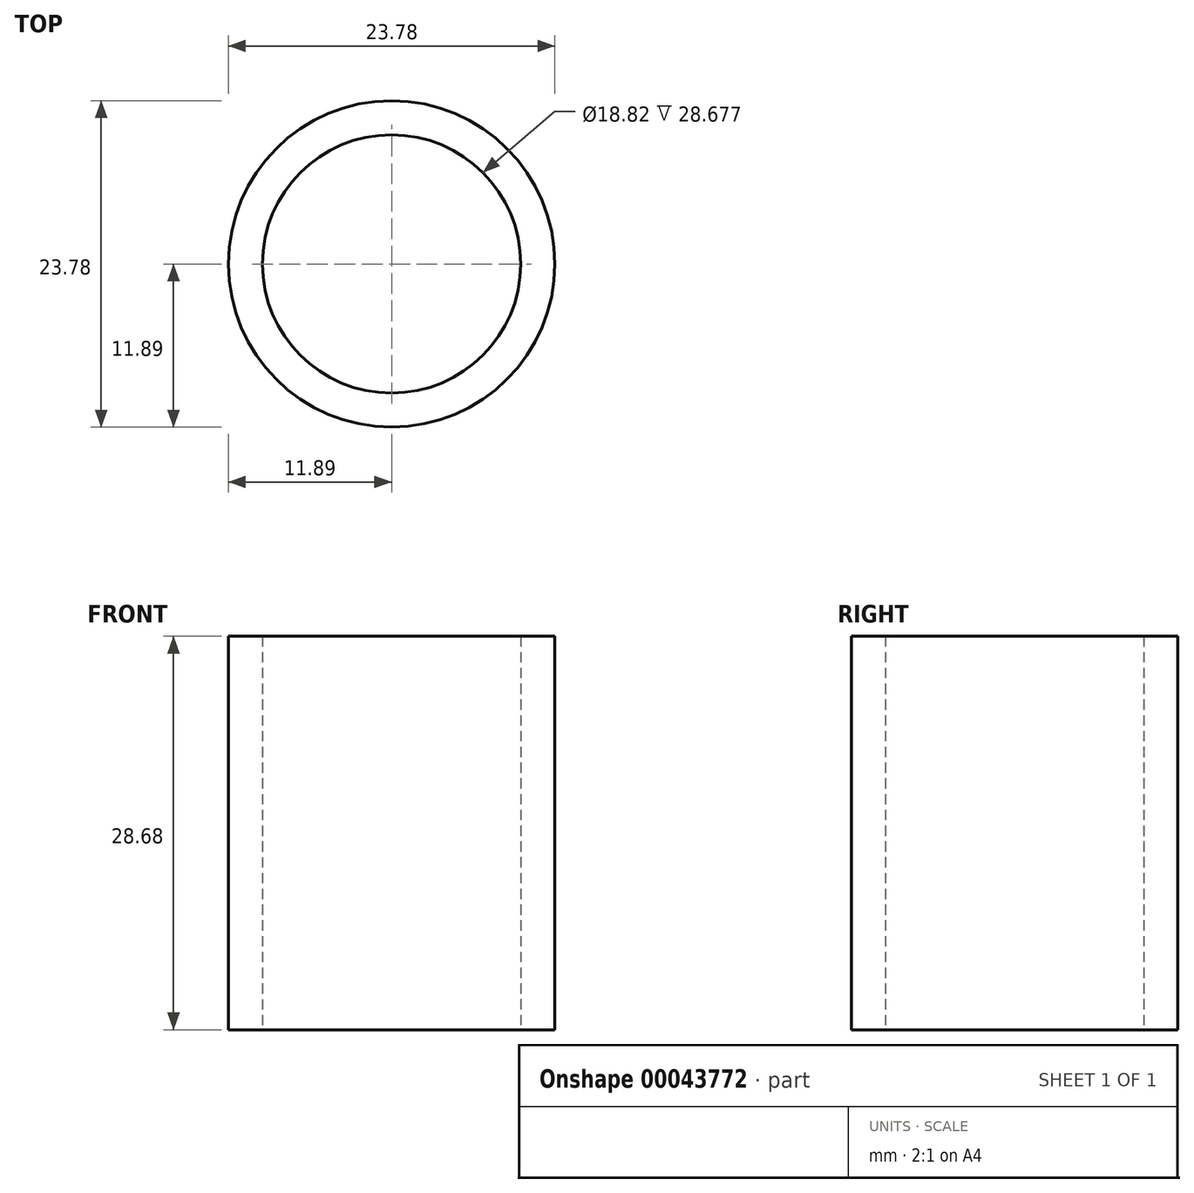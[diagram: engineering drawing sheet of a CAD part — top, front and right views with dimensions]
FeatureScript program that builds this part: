
annotation { "Feature Type Name" : "Feature", "Feature Type Description" : "" }
export const myFeature = defineFeature(function(context is Context, id is Id, definition is map)
    precondition{}
    {
        {
            var Q0;
            Q0=qCreatedBy(makeId("Front.planeOp"),FACE);
            var sketch = newSketch(context, id + "F0", { "sketchPlane" : qUnion([Q0])});
            skLineSegment(sketch, "E0", {"start": v(0, 0) * mm, "end": v(9.41, 0) * mm});
            skLineSegment(sketch, "E1", {"start": v(9.41, 0) * mm, "end": v(9.41, 28.68) * mm});
            skLineSegment(sketch, "E2", {"start": v(9.41, 28.68) * mm, "end": v(11.9, 28.68) * mm});
            skLineSegment(sketch, "E3", {"start": v(11.9, 28.68) * mm, "end": v(11.9, 0) * mm});
            skLineSegment(sketch, "E4", {"start": v(11.9, 0) * mm, "end": v(9.41, 0) * mm});
            skLineSegment(sketch, "E5", {"start": v(0, 0) * mm, "end": v(0, 28.68) * mm});
            skLineSegment(sketch, "E6", {"start": v(0, 28.68) * mm, "end": v(9.41, 28.68) * mm});
            skSolve(sketch);
        }
        {
            var Q0;
            Q0=makeQuery(id+"F0.imprint","IMPRINT",FACE,{"disambiguationData":[TD([[makeQuery(id+"F0.imprint","IMPRINT",EDGE,{"derivedFrom":sQuery(id+"F0.wireOp",EDGE,"E1")}),-1.0]])]});
            var Q1;
            Q1=sQuery(id+"F0.wireOp",EDGE,"E5");
            revolve(context, id + "F1", {"entities" : qUnion([Q0]), "axis" : qUnion([Q1]), "revolveType" : RevolveType.FULL});
        }
    });
